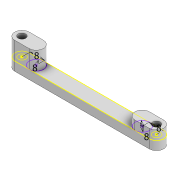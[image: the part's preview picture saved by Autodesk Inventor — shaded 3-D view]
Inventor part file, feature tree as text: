
AUTODESK INVENTOR PART (.ipt)
format: ipt  version: 2022 (Build 260153000, 153)  size: 117,760 bytes
history: native  units: mm
features: extrude x3, sketch x2, projected_geometry x1
ambient origin geometry x8: Origin, YZ Plane, XZ Plane, XY Plane, X Axis, Y Axis, Z Axis, Center Point
bodies: Solid1 (feature_tree)
feature tree (6):
  extrude  "Extrusion1"  Depth=8.0mm
  sketch  "Sketch4"  dims[d2=4.2mm d4=5.0mm d5=0.0mm d10=4.2mm d30=8.0mm d31=8.0mm d32=8.0mm d33=8.0mm d34=10.0mm d35=0.0mm d36=5.0mm d37=0.0mm]
  extrude  "Extrusion7"  Depth=5.0mm TaperAngle=0.0deg
  extrude  "Extrusion8"  Depth=5.0mm
  sketch  "Sketch1"  dims[d0=75.105mm d1=8.0mm]
  projected_geometry  "Projected Loop3"
